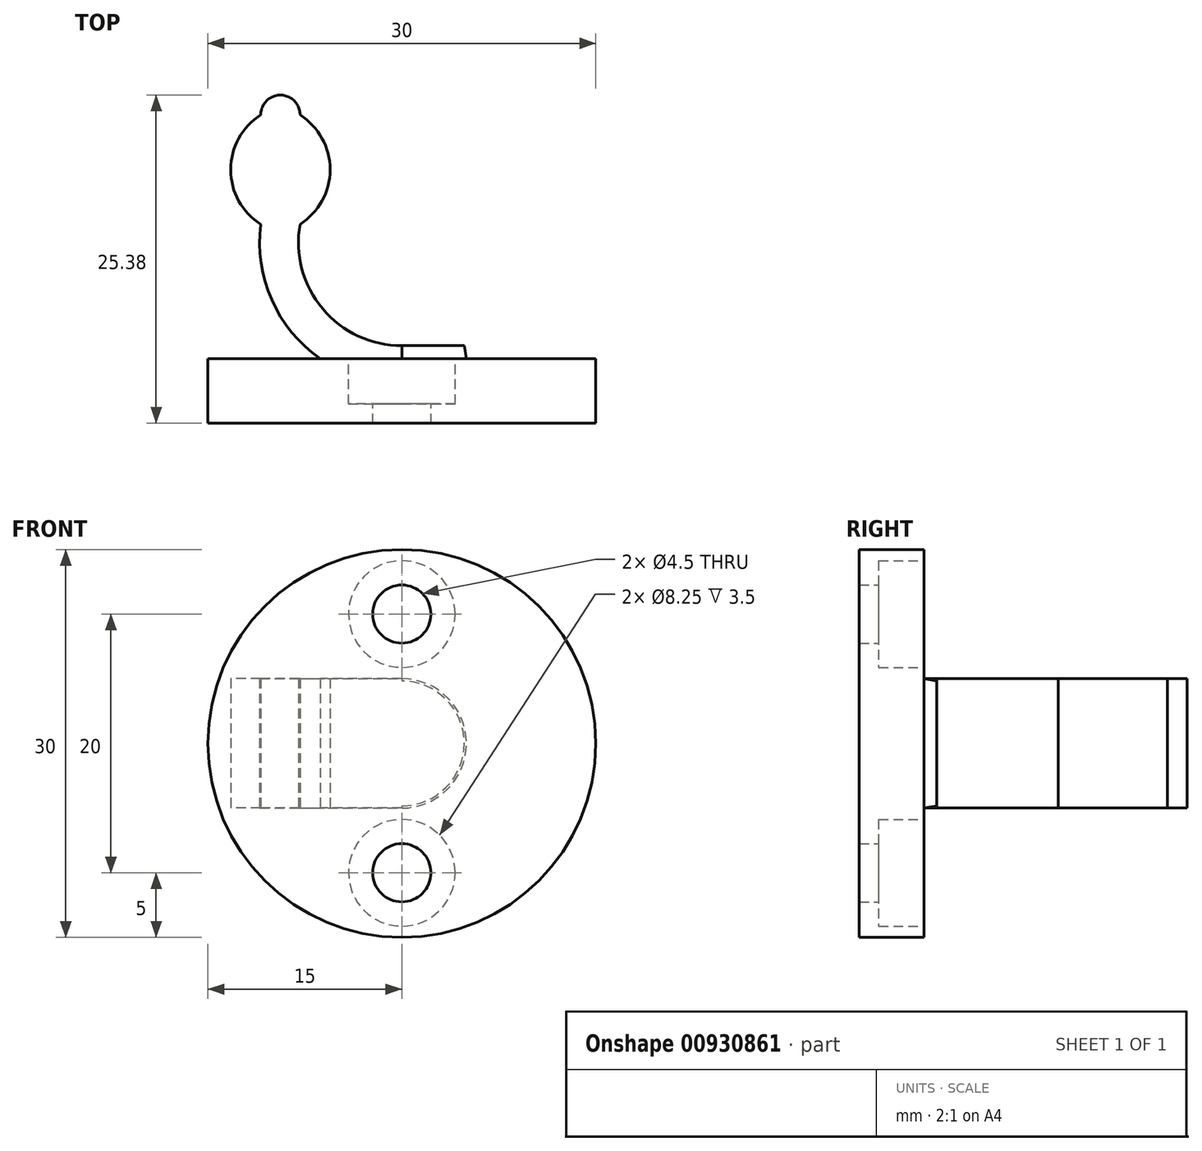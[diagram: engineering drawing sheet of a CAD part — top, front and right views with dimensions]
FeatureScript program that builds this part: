
annotation { "Feature Type Name" : "Feature", "Feature Type Description" : "" }
export const myFeature = defineFeature(function(context is Context, id is Id, definition is map)
    precondition{}
    {
        {
            var Q0;
            Q0=qCreatedBy(makeId("Top.planeOp"),FACE);
            var sketch = newSketch(context, id + "F0", { "sketchPlane" : qUnion([Q0])});
            skCircle(sketch, "E0", {"center": v(0, 0) * mm, "radius": 7.5 * mm, "construction": true});
            skLineSegment(sketch, "E1", {"start": v(7.37, 1.39) * mm, "end": v(-7.37, 1.39) * mm, "construction": true});
            skArc(sketch, "E2.0", {"start": v(7.88, 1.39) * mm, "mid": v(0, -8) * mm, "end": v(-7.88, 1.39) * mm});
            skLineSegment(sketch, "E3", {"start": v(0, 0) * mm, "end": v(-7.88, 1.39) * mm, "construction": true});
            skArc(sketch, "E4.0", {"start": v(10.91, 1.39) * mm, "mid": v(0, -11) * mm, "end": v(-10.91, 1.39) * mm});
            skLineSegment(sketch, "E5", {"start": v(7.88, 1.39) * mm, "end": v(10.91, 1.39) * mm, "construction": true});
            skLineSegment(sketch, "E6", {"start": v(-10.91, 1.39) * mm, "end": v(-7.88, 1.39) * mm, "construction": true});
            skLineSegment(sketch, "E7", {"start": v(-4.82, -8) * mm, "end": v(-5, -9) * mm});
            skLineSegment(sketch, "E8", {"start": v(-5, -9) * mm, "end": v(-15, -9) * mm});
            skLineSegment(sketch, "E9", {"start": v(-15, -9) * mm, "end": v(-15, -14) * mm});
            skLineSegment(sketch, "E10", {"start": v(-15, -14) * mm, "end": v(0, -14) * mm});
            skLineSegment(sketch, "E11", {"start": v(0, -14) * mm, "end": v(0, -8) * mm});
            skLineSegment(sketch, "E12", {"start": v(0, -8) * mm, "end": v(-4.82, -8) * mm});
            skArc(sketch, "E13", {"start": v(-7.88, 1.39) * mm, "mid": v(-5.55, 5.62) * mm, "end": v(-7.88, 9.84) * mm});
            skLineSegment(sketch, "E14", {"start": v(-9.4, 9.84) * mm, "end": v(-9.4, 1.39) * mm, "construction": true});
            skArc(sketch, "E15.MirrorCS", {"start": v(-10.91, 1.39) * mm, "mid": v(-13.24, 5.62) * mm, "end": v(-10.91, 9.84) * mm});
            skArc(sketch, "E16.MirrorCS", {"start": v(7.88, 1.39) * mm, "mid": v(5.55, 5.62) * mm, "end": v(7.88, 9.84) * mm});
            skArc(sketch, "E17.MirrorCS", {"start": v(10.91, 1.39) * mm, "mid": v(13.24, 5.62) * mm, "end": v(10.91, 9.84) * mm});
            skLineSegment(sketch, "E18.MirrorCS", {"start": v(9.4, 9.84) * mm, "end": v(9.4, 1.39) * mm, "construction": true});
            skArc(sketch, "E19", {"start": v(-7.88, 9.84) * mm, "mid": v(-9.4, 11.38) * mm, "end": v(-10.91, 9.84) * mm});
            skArc(sketch, "E20.MirrorCS", {"start": v(7.88, 9.84) * mm, "mid": v(9.4, 11.38) * mm, "end": v(10.91, 9.84) * mm});
            skLineSegment(sketch, "E21", {"start": v(0, -12.86) * mm, "end": v(0, -50.45) * mm, "construction": true});
            skSolve(sketch);
        }
        {
            var Q0;
            {var subQ5=sQuery(id+"F0.wireOp",EDGE,"E16.MirrorCS");Q0=makeQuery(id+"F0.imprint","IMPRINT",FACE,{"disambiguationData":[TD([[makeQuery(id+"F0.imprint","IMPRINT",EDGE,{"derivedFrom":subQ5}),-1.0]])]});}
            var Q1;
            {var subQ0=sQuery(id+"F0.wireOp",EDGE,"E12");Q1=makeQuery(id+"F0.imprint","IMPRINT",FACE,{"disambiguationData":[TD([[makeQuery(id+"F0.imprint","IMPRINT",EDGE,{"derivedFrom":subQ0}),-1.0]])]});}
            var Q2;
            {var subQ5=sQuery(id+"F0.wireOp",EDGE,"E12");Q2=makeQuery(id+"F0.imprint","IMPRINT",FACE,{"disambiguationData":[TD([[makeQuery(id+"F0.imprint","IMPRINT",EDGE,{"derivedFrom":subQ5}),1.0]])]});}
            extrude(context, id + "F1", {"entities" : qUnion([Q0, Q1, Q2]), "endBound" : BoundingType.SYMMETRIC, "depth" : 10 * mm, "offsetDistance" : 25 * mm});
        }
        {
            var Q0;
            {var subQ0=sQuery(id+"F0.wireOp",EDGE,"E8");Q0=makeQuery(id+"F0.imprint","IMPRINT",FACE,{"disambiguationData":[TD([[makeQuery(id+"F0.imprint","IMPRINT",EDGE,{"derivedFrom":subQ0}),1.0]])]});}
            var Q1;
            Q1=sQuery(id+"F0.wireOp",EDGE,"E21");
            revolve(context, id + "F2", {"surfaceOperationType" : NewSurfaceOperationType.NEW, "entities" : qUnion([Q0]), "axis" : qUnion([Q1]), "revolveType" : RevolveType.FULL});
        }
        {
            var Q0;
            Q0=makeQuery(id+"F1.opExtrude","SWEPT_BODY",BODY,{"disambiguationData":[OSD([sQuery(id+"F0.wireOp",EDGE,"E2.0"),sQuery(id+"F0.wireOp",EDGE,"E4.0"),sQuery(id+"F0.wireOp",EDGE,"E13"),sQuery(id+"F0.wireOp",EDGE,"E15.MirrorCS"),sQuery(id+"F0.wireOp",EDGE,"E16.MirrorCS"),sQuery(id+"F0.wireOp",EDGE,"E17.MirrorCS"),sQuery(id+"F0.wireOp",EDGE,"E19"),sQuery(id+"F0.wireOp",EDGE,"E20.MirrorCS")])]});
            var Q1;
            Q1=makeQuery(id+"F2.opRevolve","SWEPT_BODY",BODY,{"disambiguationData":[OSD([sQuery(id+"F0.wireOp",EDGE,"E4.0"),sQuery(id+"F0.wireOp",EDGE,"E7"),sQuery(id+"F0.wireOp",EDGE,"E8"),sQuery(id+"F0.wireOp",EDGE,"E9"),sQuery(id+"F0.wireOp",EDGE,"E10"),sQuery(id+"F0.wireOp",EDGE,"E11")])]});
            booleanBodies(context, id + "F3", {"operationType" : BooleanOperationType.UNION, "tools" : qUnion([Q0, Q1])});
        }
        {
            var Q0;
            Q0=makeQuery(id+"F2.opRevolve","SWEPT_FACE",FACE,{"disambiguationData":[OSD([sQuery(id+"F0.wireOp",EDGE,"E8")])]});
            var sketch = newSketch(context, id + "F4", { "sketchPlane" : qUnion([Q0])});
            skLineSegment(sketch, "E22", {"start": v(0, -15) * mm, "end": v(0, -5) * mm, "construction": true});
            skPoint(sketch, "E23", {"position": v(0, -10) * mm});
            skLineSegment(sketch, "E24.MirrorCS", {"start": v(0, 15) * mm, "end": v(0, 5) * mm, "construction": true});
            skPoint(sketch, "E25.MirrorP", {"position": v(0, 10) * mm});
            skSolve(sketch);
        }
        {
            var Q0;
            Q0=sQuery(id+"F4.wireOp",VERTEX,"E23");
            var Q1;
            Q1=sQuery(id+"F4.wireOp",VERTEX,"E25.MirrorP");
            var Q2;
            Q2=makeQuery(id+"F1.opExtrude","SWEPT_BODY",BODY,{"disambiguationData":[OSD([sQuery(id+"F0.wireOp",EDGE,"E2.0"),sQuery(id+"F0.wireOp",EDGE,"E4.0"),sQuery(id+"F0.wireOp",EDGE,"E13"),sQuery(id+"F0.wireOp",EDGE,"E15.MirrorCS"),sQuery(id+"F0.wireOp",EDGE,"E16.MirrorCS"),sQuery(id+"F0.wireOp",EDGE,"E17.MirrorCS"),sQuery(id+"F0.wireOp",EDGE,"E19"),sQuery(id+"F0.wireOp",EDGE,"E20.MirrorCS")])]});
            hole(context, id + "F5", {"style" : HoleStyle.C_BORE, "endStyle" : HoleEndStyle.THROUGH, "holeDiameter" : 4.5 * mm, "cBoreDiameter" : 8.25 * mm, "cBoreDepth" : 3.5 * mm, "majorDiameter" : 4 * mm, "isTappedThrough" : true, "tappedDepth" : 12 * mm, "tapClearance" : 3, "locations" : qUnion([Q0, Q1]), "scope" : qUnion([Q2])});
        }
    });
